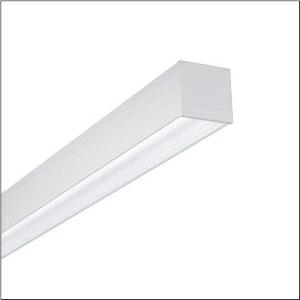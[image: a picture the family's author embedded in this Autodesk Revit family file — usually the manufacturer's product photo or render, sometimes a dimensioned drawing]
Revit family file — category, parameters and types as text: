
# Revit family: silica_r_5mx31bd2e4a_4c21
name_source: partatom
category: Lighting Fixtures
units: mm (PartAtom-declared; Revit-internal decimal feet)

## family parameters
Cut with Voids When Loaded = No
Host = Face
Light Source = No
Part Type = Normal
Room Calculation Point = No
Round Connector Dimension = Use Diameter
Shared = No

## types (1)
- --- (1 x LED, 14160 lm, 92.6 W, 4000K)
    Apparent Load = 93 VA
    CIE Flux Codes = 82 97 100 70 100
    Color Rendering = 80
    Color Temperature = 4000K
    Default Elevation = 1800 mm
    Description = Silica®, office luminaire, of aluminium, light emission: direct/indirect distribution, primary light characteristic: symmetric, installation type: suspended mounting, LED rated luminous flux: 14.160 lm, light colour: 840, colour temperature: 4000K, control gear: ECG DALI, with terminal, 3+2-pole, max. 2.5mm², mains connection: 230V, AC, 50/60Hz, connection cable inclusive, cable length: 1,5 m, rated input power: 93W, luminaire housing, of aluminium, anodised, silver, length: 2.844 mm, width: 65 mm, height: 64mm, protection rating (complete): IP20, insulation class (complete): insulation class I (protective earthing), certification: CE, permissible ambient temperature for indoor applications: 0..+35°C, standard: EN 50419, packaging unit: 1 piece
    Height = 64 mm
    Lamp = 1 x LED
    Lamp Light Flux = 14160 lm
    Lamp Power = 92.6 W
    Lamp count = 1
    Length = 2845 mm
    Luminous efficacy = 153 lm/W
    Manufacturer = Siteco
    ModVariant = No
    Model = 5MX31BD2E4A
    Mounting Place = Ceiling
    Mounting Type = Pendant
    Number of Poles = 1
    OnlyDefault = Yes
    Power Factor = 1
    Product Name = Silica®
    Product group = office luminaire | ceiling pendant
    ProductGroupID = 905
    Protection Class = Protection class I
    Protection Degree = IP 20
    RLX_Detail_Level = 1
    RlxData = <blob elided: 32757 chars, md5=c4c74456>
    Socket = socket
    Standby Power = 0 W
    System Light Flux = 14160 lm
    System Power = 93 W
    Type Comments = factory setting: direct and indirect light
    Type Image = l_1005409.jpg
    URL = http://relux.com
    VarID = @adj_131720
    Voltage = 0 V
    Weight = 0.00 kg
    Width = 66 mm

## geometry (parser evidence)
native form markers: Blend x4, Sweep x12
no freeform markers — native parametric forms only
